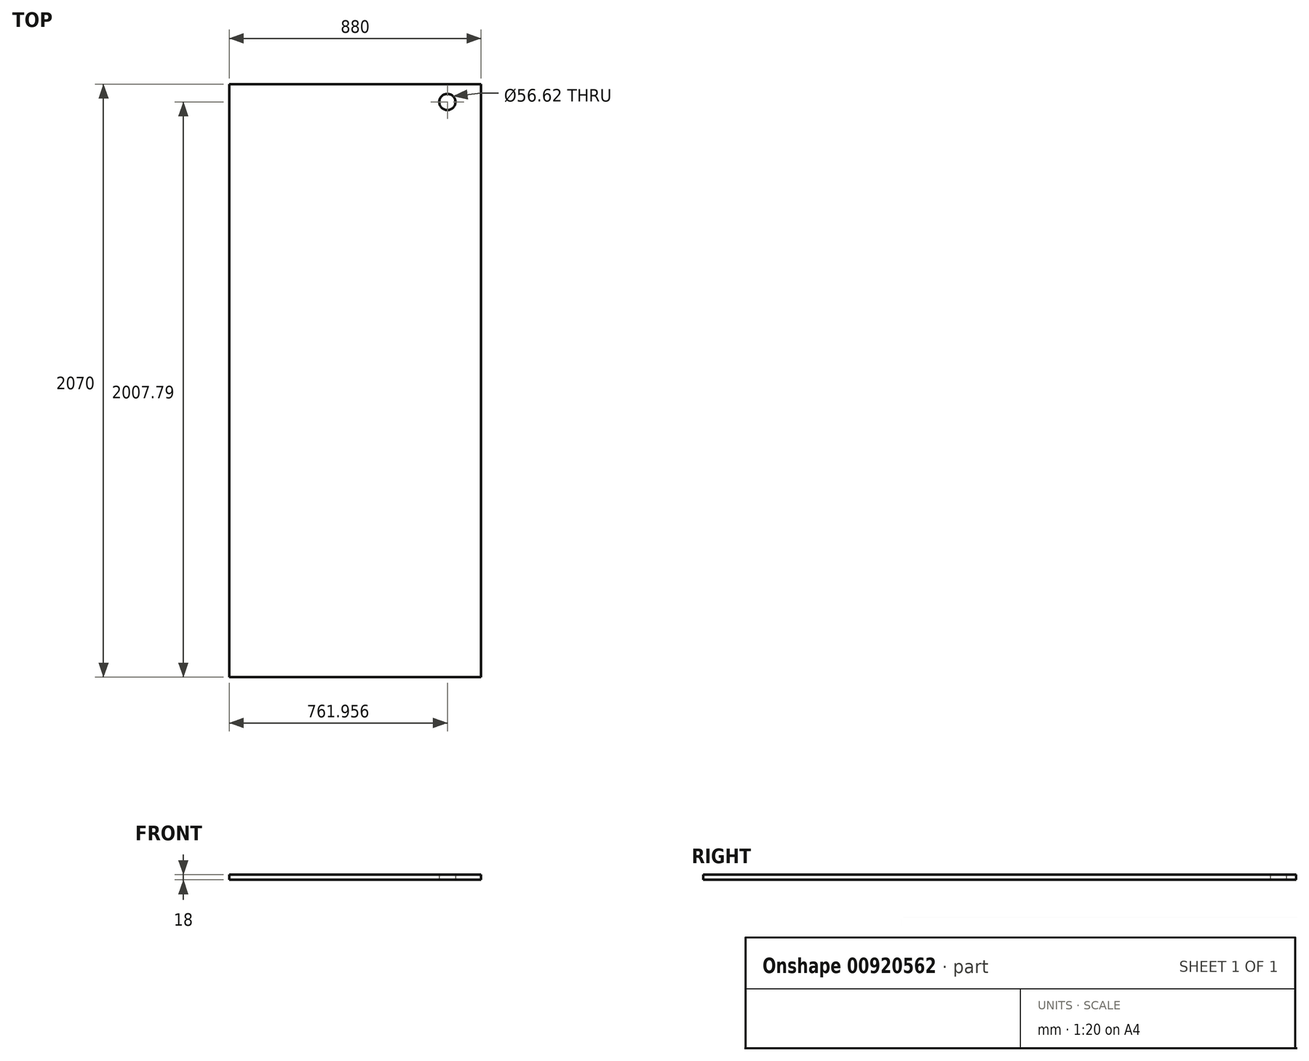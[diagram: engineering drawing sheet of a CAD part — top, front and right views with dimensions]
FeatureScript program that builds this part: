
annotation { "Feature Type Name" : "Feature", "Feature Type Description" : "" }
export const myFeature = defineFeature(function(context is Context, id is Id, definition is map)
    precondition{}
    {
        {
            var Q0;
            Q0=qCreatedBy(makeId("Top.planeOp"),FACE);
            var sketch = newSketch(context, id + "F0", { "sketchPlane" : qUnion([Q0])});
            skLineSegment(sketch, "E0.bottom", {"start": v(440, -1035) * mm, "end": v(-440, -1035) * mm});
            skLineSegment(sketch, "E0.top", {"start": v(440, 1035) * mm, "end": v(-440, 1035) * mm});
            skLineSegment(sketch, "E0.left", {"start": v(440, -1035) * mm, "end": v(440, 1035) * mm});
            skLineSegment(sketch, "E0.right", {"start": v(-440, -1035) * mm, "end": v(-440, 1035) * mm});
            skPoint(sketch, "E0.middle", {"position": v(0, 0) * mm});
            skSolve(sketch);
        }
        {
            var Q0;
            Q0=qSketchRegion(id+"F0",true);
            extrude(context, id + "F1", {"entities" : qUnion([Q0]), "depth" : 18 * mm, "offsetDistance" : 25 * mm, "symmetric" : true});
        }
        {
            var Q0;
            Q0=makeQuery(id+"F1.opExtrude","CAP_FACE",FACE,{"disambiguationData":[OSD([sQuery(id+"F0.wireOp",EDGE,"E0.bottom"),sQuery(id+"F0.wireOp",EDGE,"E0.top"),sQuery(id+"F0.wireOp",EDGE,"E0.left"),sQuery(id+"F0.wireOp",EDGE,"E0.right")])],"isStart":true});
            var sketch = newSketch(context, id + "F2", { "sketchPlane" : qUnion([Q0])});
            skCircle(sketch, "E1", {"center": v(321.96, -972.79) * mm, "radius": 28.3 * mm});
            skSolve(sketch);
        }
        {
            var Q0;
            Q0=qSketchRegion(id+"F2",true);
            extrude(context, id + "F3", {"entities" : qUnion([Q0]), "operationType" : NewBodyOperationType.REMOVE, "oppositeDirection" : true, "depth" : 18 * mm, "offsetDistance" : 25 * mm});
        }
    });
